FCSTD DOCUMENT  (FreeCAD 0.18.4R)
Label: servo_mkii
License: All rights reserved
LicenseURL: http://en.wikipedia.org/wiki/All_rights_reserved
objects: Sketcher::SketchObject×1
note: 1 computed .brp shape members not serialized (recipe doc carries the construction recipe); baked Part::Feature solids carry a one-line shape summary decoded from their .brp

FEATURE [Sketcher::SketchObject] Sketch
  sketch-geometry (163):
    g0: LineSegment StartX=-37.4556 StartY=-13.9835 StartZ=0 EndX=-37.4556 EndY=24.5165 EndZ=0
    g1: ArcOfCircle CenterX=-36.4556 CenterY=24.5165 CenterZ=0 NormalX=0 NormalY=0 NormalZ=1 AngleXU=0 Radius=1 StartAngle=1.5708 EndAngle=3.14159
    g2: ArcOfCircle CenterX=-36.4556 CenterY=-13.9835 CenterZ=0 NormalX=0 NormalY=0 NormalZ=1 AngleXU=0 Radius=1 StartAngle=3.14159 EndAngle=4.71239
    g3: LineSegment StartX=-36.4556 StartY=-14.9835 StartZ=0 EndX=-36.4556 EndY=-21.2835 EndZ=0
    g4: ArcOfCircle CenterX=-35.4557 CenterY=-21.2997 CenterZ=0 NormalX=0 NormalY=0 NormalZ=1 AngleXU=0 Radius=1 StartAngle=3.12536 EndAngle=4.69615
    g5: LineSegment StartX=-35.472 StartY=-22.2996 StartZ=0 EndX=-33.722 EndY=-22.2996 EndZ=0
    g6: LineSegment StartX=-33.722 StartY=-22.2996 StartZ=0 EndX=-33.722 EndY=-21.6996 EndZ=0
    g7: ArcOfCircle CenterX=-32.4638 CenterY=-19.8343 CenterZ=0 NormalX=0 NormalY=0 NormalZ=1 AngleXU=0 Radius=2.25 StartAngle=5.3058 EndAngle=10.4022
    g8: LineSegment [constr] StartX=-33.722 StartY=-21.6996 StartZ=0 EndX=-31.2056 EndY=-21.6996 EndZ=0
    g9: LineSegment StartX=-31.2056 StartY=-21.6996 StartZ=0 EndX=-31.2056 EndY=-22.2996 EndZ=0
    g10: LineSegment [constr] StartX=-33.722 StartY=-22.2996 StartZ=0 EndX=-31.2056 EndY=-22.2996 EndZ=0
    g11: LineSegment StartX=-31.2056 StartY=-22.2996 StartZ=0 EndX=-27.4556 EndY=-22.2996 EndZ=0
    g12: LineSegment [constr] StartX=-36.4556 StartY=-14.9835 StartZ=0 EndX=-28.4556 EndY=-14.9835 EndZ=0
    g13: LineSegment StartX=-28.4556 StartY=-14.9835 StartZ=0 EndX=-28.4556 EndY=-17.9835 EndZ=0
    g14: ArcOfCircle CenterX=-27.4556 CenterY=-17.9835 CenterZ=0 NormalX=0 NormalY=0 NormalZ=1 AngleXU=0 Radius=1 StartAngle=3.14159 EndAngle=4.71239
    g15: LineSegment [constr] StartX=-28.4556 StartY=-17.9835 StartZ=0 EndX=-27.4556 EndY=-17.9835 EndZ=0
    g16: LineSegment [constr] StartX=-27.4556 StartY=-18.9835 StartZ=0 EndX=-27.4556 EndY=-22.2996 EndZ=0
    g17: LineSegment StartX=-28.4556 StartY=-14.9835 StartZ=0 EndX=-27.4556 EndY=-14.9835 EndZ=0
    g18: LineSegment [constr] StartX=-27.4556 StartY=-18.9835 StartZ=0 EndX=-27.4556 EndY=-14.9835 EndZ=0
    g19: LineSegment [constr] StartX=-27.4556 StartY=-14.9835 StartZ=0 EndX=-27.4556 EndY=-4.6835 EndZ=0
    g20: LineSegment [constr] StartX=-27.4556 StartY=-4.6835 StartZ=0 EndX=-37.4556 EndY=-4.6835 EndZ=0
    g21: GeomPoint X=-27.4556 Y=-12.9335 Z=0
    g22: GeomPoint X=-27.4556 Y=-12.0335 Z=0
    g23: ArcOfCircle CenterX=-27.4556 CenterY=-12.6335 CenterZ=0 NormalX=0 NormalY=0 NormalZ=1 AngleXU=0 Radius=0.3 StartAngle=3.14159 EndAngle=4.71239
    g24: LineSegment StartX=-27.7556 StartY=-12.6335 StartZ=0 EndX=-27.7556 EndY=-12.3335 EndZ=0
    g25: ArcOfCircle CenterX=-27.4556 CenterY=-12.3335 CenterZ=0 NormalX=0 NormalY=0 NormalZ=1 AngleXU=0 Radius=0.3 StartAngle=1.5708 EndAngle=3.14159
    g26: ArcOfCircle [constr] CenterX=-27.4677 CenterY=-4.6835 CenterZ=0 NormalX=0 NormalY=0 NormalZ=1 AngleXU=0 Radius=7.35001 StartAngle=4.19043 EndAngle=4.71403
    g27: LineSegment StartX=-31.4668 StartY=-11.115 StartZ=0 EndX=-31.6319 EndY=-11.4794 EndZ=0
    g28: LineSegment [constr] StartX=-31.4668 StartY=-11.115 StartZ=0 EndX=-31.2846 EndY=-11.1976 EndZ=0
    g29: ArcOfCircle CenterX=-31.2846 CenterY=-11.1976 CenterZ=0 NormalX=0 NormalY=0 NormalZ=1 AngleXU=0 Radius=0.2 StartAngle=5.85782 EndAngle=8.99941
    g30: LineSegment [constr] StartX=-31.2846 StartY=-11.1976 StartZ=0 EndX=-31.4497 EndY=-11.5619 EndZ=0
    g31: LineSegment [constr] StartX=-31.6319 StartY=-11.4794 StartZ=0 EndX=-31.4497 EndY=-11.5619 EndZ=0
    g32: ArcOfCircle CenterX=-31.4497 CenterY=-11.5619 CenterZ=0 NormalX=0 NormalY=0 NormalZ=1 AngleXU=0 Radius=0.2 StartAngle=2.71623 EndAngle=5.85782
    g33: LineSegment StartX=-31.2675 StartY=-11.6445 StartZ=0 EndX=-31.1025 EndY=-11.2801 EndZ=0
    g34: ArcOfCircle [constr] CenterX=-27.4677 CenterY=-4.6835 CenterZ=0 NormalX=0 NormalY=0 NormalZ=1 AngleXU=0 Radius=7.35001 StartAngle=3.66683 EndAngle=4.19043
    g35: LineSegment [constr] StartX=-33.8269 StartY=-8.36894 StartZ=0 EndX=-34.5191 EndY=-8.77007 EndZ=0
    g36: GeomPoint X=-34 Y=-8.46922 Z=0
    g37: ArcOfCircle CenterX=-34 CenterY=-8.46922 CenterZ=0 NormalX=0 NormalY=0 NormalZ=1 AngleXU=0 Radius=0.2 StartAngle=5.2351 EndAngle=8.37669
    g38: LineSegment StartX=-34.0998 StartY=-8.29593 StartZ=0 EndX=-34.4464 EndY=-8.49562 EndZ=0
    g39: LineSegment StartX=-33.9001 StartY=-8.64252 StartZ=0 EndX=-34.2467 EndY=-8.84221 EndZ=0
    g40: LineSegment [constr] StartX=-34.4464 StartY=-8.49562 StartZ=0 EndX=-34.2467 EndY=-8.84221 EndZ=0
    g41: ArcOfCircle CenterX=-34.3465 CenterY=-8.66891 CenterZ=0 NormalX=0 NormalY=0 NormalZ=1 AngleXU=0 Radius=0.2 StartAngle=2.0935 EndAngle=5.2351
    g42: ArcOfCircle [constr] CenterX=-27.4677 CenterY=-4.6835 CenterZ=0 NormalX=0 NormalY=0 NormalZ=1 AngleXU=0 Radius=7.35001 StartAngle=3.14159 EndAngle=3.66683
    g43: GeomPoint X=-34.8177 Y=-4.6835 Z=0
    g44: GeomPoint X=-35.7177 Y=-4.6835 Z=0
    g45: ArcOfCircle CenterX=-35.1487 CenterY=-4.6835 CenterZ=0 NormalX=0 NormalY=0 NormalZ=1 AngleXU=0 Radius=0.3 StartAngle=4.71239 EndAngle=7.85398
    g46: LineSegment StartX=-35.1487 StartY=-4.3835 StartZ=0 EndX=-35.4487 EndY=-4.3835 EndZ=0
    g47: LineSegment [constr] StartX=-35.4487 StartY=-4.3835 StartZ=0 EndX=-35.4487 EndY=-4.6835 EndZ=0
    g48: ArcOfCircle CenterX=-35.4487 CenterY=-4.6835 CenterZ=0 NormalX=0 NormalY=0 NormalZ=1 AngleXU=0 Radius=0.3 StartAngle=1.5708 EndAngle=4.71239
    g49: LineSegment StartX=-35.4487 StartY=-4.9835 StartZ=0 EndX=-35.1487 EndY=-4.9835 EndZ=0
    g50: ArcOfCircle [constr] CenterX=-27.4677 CenterY=-4.6835 CenterZ=0 NormalX=0 NormalY=0 NormalZ=1 AngleXU=0 Radius=7.35001 StartAngle=2.61799 EndAngle=3.14159
    g51: GeomPoint X=-34.0061 Y=-0.908499 Z=0
    g52: ArcOfCircle CenterX=-34.0061 CenterY=-0.908499 CenterZ=0 NormalX=0 NormalY=0 NormalZ=1 AngleXU=0 Radius=0.2 StartAngle=4.18878 EndAngle=7.33037
    g53: LineSegment StartX=-33.9061 StartY=-0.735295 StartZ=0 EndX=-34.2526 EndY=-0.535291 EndZ=0
    g54: ArcOfCircle CenterX=-34.3526 CenterY=-0.708495 CenterZ=0 NormalX=0 NormalY=0 NormalZ=1 AngleXU=0 Radius=0.2 StartAngle=1.04719 EndAngle=4.18878
    g55: LineSegment StartX=-34.4526 StartY=-0.881699 StartZ=0 EndX=-34.1061 EndY=-1.0817 EndZ=0
    g56: ArcOfCircle [constr] CenterX=-27.4677 CenterY=-4.6835 CenterZ=0 NormalX=0 NormalY=0 NormalZ=1 AngleXU=0 Radius=7.35001 StartAngle=2.09439 EndAngle=2.61799
    g57: ArcOfCircle CenterX=-31.2427 CenterY=1.85499 CenterZ=0 NormalX=0 NormalY=0 NormalZ=1 AngleXU=0 Radius=0.2 StartAngle=3.66593 EndAngle=6.80752
    g58: LineSegment StartX=-31.0695 StartY=1.95512 StartZ=0 EndX=-31.2698 EndY=2.30138 EndZ=0
    g59: ArcOfCircle CenterX=-31.4429 CenterY=2.20126 CenterZ=0 NormalX=0 NormalY=0 NormalZ=1 AngleXU=0 Radius=0.2 StartAngle=0.524334 EndAngle=3.66593
    g60: LineSegment StartX=-31.616 StartY=2.10113 StartZ=0 EndX=-31.4158 EndY=1.75487 EndZ=0
    g61: ArcOfCircle CenterX=-27.4556 CenterY=-4.70855 CenterZ=0 NormalX=0 NormalY=0 NormalZ=1 AngleXU=0 Radius=3 StartAngle=1.5708 EndAngle=4.71239
    g62: ArcOfCircle CenterX=-27.4556 CenterY=-4.68351 CenterZ=0 NormalX=0 NormalY=0 NormalZ=1 AngleXU=0 Radius=5.5 StartAngle=1.5708 EndAngle=4.71239
    g63: ArcOfCircle CenterX=-27.4556 CenterY=-4.70855 CenterZ=0 NormalX=0 NormalY=0 NormalZ=1 AngleXU=0 Radius=7.3 StartAngle=1.5708 EndAngle=4.71239
    g64: LineSegment [constr] StartX=-27.4556 StartY=-4.70855 StartZ=0 EndX=-27.4556 EndY=-1.70855 EndZ=0
    g65: LineSegment [constr] StartX=-27.4556 StartY=-1.70855 StartZ=0 EndX=-27.4556 EndY=0.816495 EndZ=0
    g66: LineSegment [constr] StartX=-27.4556 StartY=0.816495 StartZ=0 EndX=-27.4556 EndY=2.59145 EndZ=0
    g67: LineSegment StartX=-36.4556 StartY=25.5165 StartZ=0 EndX=-36.4556 EndY=30.8165 EndZ=0
    g68: ArcOfCircle CenterX=-35.4556 CenterY=30.8165 CenterZ=0 NormalX=0 NormalY=0 NormalZ=1 AngleXU=0 Radius=1 StartAngle=1.5708 EndAngle=3.14159
    g69: LineSegment StartX=-35.4556 StartY=31.8165 StartZ=0 EndX=-33.7056 EndY=31.8165 EndZ=0
    g70: LineSegment StartX=-33.7056 StartY=31.8165 StartZ=0 EndX=-33.7056 EndY=31.2165 EndZ=0
    g71: ArcOfCircle CenterX=-32.4474 CenterY=29.3512 CenterZ=0 NormalX=0 NormalY=0 NormalZ=1 AngleXU=0 Radius=2.25 StartAngle=2.16421 EndAngle=7.26057
    g72: LineSegment [constr] StartX=-33.7056 StartY=31.2165 StartZ=0 EndX=-31.1892 EndY=31.2165 EndZ=0
    g73: LineSegment StartX=-31.1892 StartY=31.2165 StartZ=0 EndX=-31.1892 EndY=31.8165 EndZ=0
    g74: LineSegment [constr] StartX=-33.7056 StartY=31.8165 StartZ=0 EndX=-31.1892 EndY=31.8165 EndZ=0
    g75: LineSegment StartX=-31.1892 StartY=31.8165 StartZ=0 EndX=-27.4392 EndY=31.8165 EndZ=0
    g76: LineSegment [constr] StartX=-36.4556 StartY=25.5165 StartZ=0 EndX=-28.4556 EndY=25.5165 EndZ=0
    g77: LineSegment StartX=-28.4556 StartY=25.5165 StartZ=0 EndX=-28.4556 EndY=28.5165 EndZ=0
    g78: LineSegment [constr] StartX=-28.4556 StartY=28.5165 StartZ=0 EndX=-27.4392 EndY=28.5165 EndZ=0
    g79: ArcOfCircle CenterX=-27.4392 CenterY=28.5165 CenterZ=0 NormalX=0 NormalY=0 NormalZ=1 AngleXU=0 Radius=1.01637 StartAngle=1.5708 EndAngle=3.14159
    g80: LineSegment StartX=-28.4556 StartY=25.5165 StartZ=0 EndX=-27.4392 EndY=25.5165 EndZ=0
    g81: LineSegment StartX=-17.4308 StartY=-13.9746 StartZ=0 EndX=-17.4308 EndY=24.5165 EndZ=0
    g82: ArcOfCircle CenterX=-18.4308 CenterY=24.5165 CenterZ=0 NormalX=0 NormalY=0 NormalZ=1 AngleXU=0 Radius=1 StartAngle=-7.1e-15 EndAngle=1.5708
    g83: ArcOfCircle CenterX=-18.4308 CenterY=-13.9746 CenterZ=0 NormalX=0 NormalY=0 NormalZ=1 AngleXU=0 Radius=1 StartAngle=4.71239 EndAngle=6.28319
    g84: LineSegment StartX=-18.4308 StartY=-14.9746 StartZ=0 EndX=-18.4308 EndY=-21.2746 EndZ=0
    g85: ArcOfCircle CenterX=-19.4307 CenterY=-21.2909 CenterZ=0 NormalX=0 NormalY=0 NormalZ=1 AngleXU=0 Radius=1 StartAngle=4.72863 EndAngle=6.29942
    g86: LineSegment StartX=-19.4145 StartY=-22.2907 StartZ=0 EndX=-21.1645 EndY=-22.2907 EndZ=0
    g87: LineSegment StartX=-21.1645 StartY=-22.2907 StartZ=0 EndX=-21.1645 EndY=-21.6907 EndZ=0
    g88: ArcOfCircle CenterX=-22.4227 CenterY=-19.8254 CenterZ=0 NormalX=0 NormalY=0 NormalZ=1 AngleXU=0 Radius=2.25 StartAngle=5.3058 EndAngle=10.4022
    g89: LineSegment [constr] StartX=-21.1645 StartY=-21.6907 StartZ=0 EndX=-23.6808 EndY=-21.6907 EndZ=0
    g90: LineSegment StartX=-23.6808 StartY=-21.6907 StartZ=0 EndX=-23.6808 EndY=-22.2907 EndZ=0
    g91: LineSegment [constr] StartX=-21.1645 StartY=-22.2907 StartZ=0 EndX=-23.6808 EndY=-22.2907 EndZ=0
    g92: LineSegment StartX=-23.6808 StartY=-22.2907 StartZ=0 EndX=-27.4308 EndY=-22.2907 EndZ=0
    g93: LineSegment [constr] StartX=-18.4308 StartY=-14.9746 StartZ=0 EndX=-26.4308 EndY=-14.9746 EndZ=0
    g94: LineSegment StartX=-26.4308 StartY=-14.9746 StartZ=0 EndX=-26.4308 EndY=-17.9746 EndZ=0
    g95: ArcOfCircle CenterX=-27.4308 CenterY=-17.9746 CenterZ=0 NormalX=0 NormalY=0 NormalZ=1 AngleXU=0 Radius=1 StartAngle=4.71239 EndAngle=6.28319
    g96: LineSegment [constr] StartX=-26.4308 StartY=-17.9746 StartZ=0 EndX=-27.4308 EndY=-17.9746 EndZ=0
    g97: LineSegment [constr] StartX=-27.4308 StartY=-18.9746 StartZ=0 EndX=-27.4308 EndY=-22.2907 EndZ=0
    g98: LineSegment StartX=-26.4308 StartY=-14.9746 StartZ=0 EndX=-27.4308 EndY=-14.9746 EndZ=0
    g99: LineSegment [constr] StartX=-27.4308 StartY=-18.9746 StartZ=0 EndX=-27.4308 EndY=-14.9746 EndZ=0
    g100: LineSegment [constr] StartX=-27.4308 StartY=-14.9746 StartZ=0 EndX=-27.4308 EndY=-4.67462 EndZ=0
    g101: LineSegment [constr] StartX=-27.4308 StartY=-4.67462 StartZ=0 EndX=-17.4308 EndY=-4.67462 EndZ=0
    g102: GeomPoint X=-27.4308 Y=-12.9246 Z=0
    g103: GeomPoint X=-27.4308 Y=-12.0246 Z=0
    g104: ArcOfCircle CenterX=-27.4308 CenterY=-12.6246 CenterZ=0 NormalX=0 NormalY=0 NormalZ=1 AngleXU=0 Radius=0.3 StartAngle=4.71239 EndAngle=6.28319
    g105: LineSegment StartX=-27.1308 StartY=-12.6246 StartZ=0 EndX=-27.1308 EndY=-12.3246 EndZ=0
    g106: ArcOfCircle CenterX=-27.4308 CenterY=-12.3246 CenterZ=0 NormalX=0 NormalY=0 NormalZ=1 AngleXU=0 Radius=0.3 StartAngle=0 EndAngle=1.5708
    g107: ArcOfCircle [constr] CenterX=-27.4188 CenterY=-4.67462 CenterZ=0 NormalX=0 NormalY=0 NormalZ=1 AngleXU=0 Radius=7.35001 StartAngle=4.71075 EndAngle=5.23435
    g108: LineSegment StartX=-23.4196 StartY=-11.1062 StartZ=0 EndX=-23.2546 EndY=-11.4705 EndZ=0
    g109: LineSegment [constr] StartX=-23.4196 StartY=-11.1062 StartZ=0 EndX=-23.6018 EndY=-11.1887 EndZ=0
    g110: ArcOfCircle CenterX=-23.6018 CenterY=-11.1887 CenterZ=0 NormalX=0 NormalY=0 NormalZ=1 AngleXU=0 Radius=0.2 StartAngle=0.425367 EndAngle=3.56696
    g111: LineSegment [constr] StartX=-23.6018 StartY=-11.1887 StartZ=0 EndX=-23.4367 EndY=-11.5531 EndZ=0
    g112: LineSegment [constr] StartX=-23.2546 StartY=-11.4705 StartZ=0 EndX=-23.4367 EndY=-11.5531 EndZ=0
    g113: ArcOfCircle CenterX=-23.4367 CenterY=-11.5531 CenterZ=0 NormalX=0 NormalY=0 NormalZ=1 AngleXU=0 Radius=0.2 StartAngle=3.56696 EndAngle=6.70855
    g114: LineSegment StartX=-23.6189 StartY=-11.6356 StartZ=0 EndX=-23.784 EndY=-11.2712 EndZ=0
    g115: ArcOfCircle [constr] CenterX=-27.4188 CenterY=-4.67462 CenterZ=0 NormalX=0 NormalY=0 NormalZ=1 AngleXU=0 Radius=7.35001 StartAngle=5.23435 EndAngle=5.75795
    g116: LineSegment [constr] StartX=-21.0595 StartY=-8.36005 StartZ=0 EndX=-20.3674 EndY=-8.76119 EndZ=0
    g117: GeomPoint X=-20.8865 Y=-8.46034 Z=0
    g118: ArcOfCircle CenterX=-20.8865 CenterY=-8.46034 CenterZ=0 NormalX=0 NormalY=0 NormalZ=1 AngleXU=0 Radius=0.2 StartAngle=1.04809 EndAngle=4.18968
    g119: LineSegment StartX=-20.7866 StartY=-8.28704 StartZ=0 EndX=-20.4401 EndY=-8.48674 EndZ=0
    g120: LineSegment StartX=-20.9863 StartY=-8.63363 StartZ=0 EndX=-20.6397 EndY=-8.83332 EndZ=0
    g121: LineSegment [constr] StartX=-20.4401 StartY=-8.48674 StartZ=0 EndX=-20.6397 EndY=-8.83332 EndZ=0
    g122: ArcOfCircle CenterX=-20.5399 CenterY=-8.66003 CenterZ=0 NormalX=0 NormalY=0 NormalZ=1 AngleXU=0 Radius=0.2 StartAngle=4.18968 EndAngle=7.33128
    g123: ArcOfCircle [constr] CenterX=-27.4188 CenterY=-4.67462 CenterZ=0 NormalX=0 NormalY=0 NormalZ=1 AngleXU=0 Radius=7.35001 StartAngle=5.75795 EndAngle=6.28319
    g124: GeomPoint X=-20.0688 Y=-4.67462 Z=0
    g125: GeomPoint X=-19.1688 Y=-4.67462 Z=0
    g126: ArcOfCircle CenterX=-19.7377 CenterY=-4.67462 CenterZ=0 NormalX=0 NormalY=0 NormalZ=1 AngleXU=0 Radius=0.3 StartAngle=1.5708 EndAngle=4.71239
    g127: LineSegment StartX=-19.7377 StartY=-4.37462 StartZ=0 EndX=-19.4377 EndY=-4.37462 EndZ=0
    g128: LineSegment [constr] StartX=-19.4377 StartY=-4.37462 StartZ=0 EndX=-19.4377 EndY=-4.67462 EndZ=0
    g129: ArcOfCircle CenterX=-19.4377 CenterY=-4.67462 CenterZ=0 NormalX=0 NormalY=0 NormalZ=1 AngleXU=0 Radius=0.3 StartAngle=4.71239 EndAngle=7.85398
    g130: LineSegment StartX=-19.4377 StartY=-4.97462 StartZ=0 EndX=-19.7377 EndY=-4.97462 EndZ=0
    g131: ArcOfCircle [constr] CenterX=-27.4188 CenterY=-4.67462 CenterZ=0 NormalX=0 NormalY=0 NormalZ=1 AngleXU=0 Radius=7.35001 StartAngle=5.03315e-07 EndAngle=0.523599
    g132: GeomPoint X=-20.8803 Y=-0.899614 Z=0
    g133: ArcOfCircle CenterX=-20.8803 CenterY=-0.899614 CenterZ=0 NormalX=0 NormalY=0 NormalZ=1 AngleXU=0 Radius=0.2 StartAngle=2.09441 EndAngle=5.236
    g134: LineSegment StartX=-20.9803 StartY=-0.72641 StartZ=0 EndX=-20.6339 EndY=-0.526407 EndZ=0
    g135: ArcOfCircle CenterX=-20.5339 CenterY=-0.699611 CenterZ=0 NormalX=0 NormalY=0 NormalZ=1 AngleXU=0 Radius=0.2 StartAngle=5.236 EndAngle=8.37759
    g136: LineSegment StartX=-20.4339 StartY=-0.872815 StartZ=0 EndX=-20.7803 EndY=-1.07282 EndZ=0
    g137: ArcOfCircle [constr] CenterX=-27.4188 CenterY=-4.67462 CenterZ=0 NormalX=0 NormalY=0 NormalZ=1 AngleXU=0 Radius=7.35001 StartAngle=0.523599 EndAngle=1.0472
    g138: ArcOfCircle CenterX=-23.6438 CenterY=1.86388 CenterZ=0 NormalX=0 NormalY=0 NormalZ=1 AngleXU=0 Radius=0.2 StartAngle=2.61726 EndAngle=5.75885
    g139: LineSegment StartX=-23.8169 StartY=1.96401 StartZ=0 EndX=-23.6167 EndY=2.31027 EndZ=0
    g140: ArcOfCircle CenterX=-23.4435 CenterY=2.21014 CenterZ=0 NormalX=0 NormalY=0 NormalZ=1 AngleXU=0 Radius=0.2 StartAngle=5.75885 EndAngle=8.90044
    g141: LineSegment StartX=-23.2704 StartY=2.11001 StartZ=0 EndX=-23.4707 EndY=1.76375 EndZ=0
    g142: ArcOfCircle CenterX=-27.4308 CenterY=-4.69967 CenterZ=0 NormalX=0 NormalY=0 NormalZ=1 AngleXU=0 Radius=3 StartAngle=4.71239 EndAngle=7.85398
    g143: ArcOfCircle CenterX=-27.4308 CenterY=-4.67462 CenterZ=0 NormalX=0 NormalY=0 NormalZ=1 AngleXU=0 Radius=5.5 StartAngle=4.71239 EndAngle=7.85398
    g144: ArcOfCircle CenterX=-27.4308 CenterY=-4.69967 CenterZ=0 NormalX=0 NormalY=0 NormalZ=1 AngleXU=0 Radius=7.3 StartAngle=4.71239 EndAngle=7.85398
    g145: LineSegment [constr] StartX=-27.4308 StartY=-4.69967 StartZ=0 EndX=-27.4308 EndY=-1.69967 EndZ=0
    g146: LineSegment [constr] StartX=-27.4308 StartY=-1.69967 StartZ=0 EndX=-27.4308 EndY=0.825379 EndZ=0
    g147: LineSegment [constr] StartX=-27.4308 StartY=0.825379 StartZ=0 EndX=-27.4308 EndY=2.60033 EndZ=0
    g148: LineSegment StartX=-18.4308 StartY=25.5165 StartZ=0 EndX=-18.4308 EndY=30.8254 EndZ=0
    g149: ArcOfCircle CenterX=-19.4308 CenterY=30.8254 CenterZ=0 NormalX=0 NormalY=0 NormalZ=1 AngleXU=0 Radius=1 StartAngle=0 EndAngle=1.5708
    g150: LineSegment StartX=-19.4308 StartY=31.8254 StartZ=0 EndX=-21.1808 EndY=31.8254 EndZ=0
    g151: LineSegment StartX=-21.1808 StartY=31.8254 StartZ=0 EndX=-21.1808 EndY=31.2254 EndZ=0
    g152: ArcOfCircle CenterX=-22.439 CenterY=29.36 CenterZ=0 NormalX=0 NormalY=0 NormalZ=1 AngleXU=0 Radius=2.25 StartAngle=2.16421 EndAngle=7.26057
    g153: LineSegment [constr] StartX=-21.1808 StartY=31.2254 StartZ=0 EndX=-23.6972 EndY=31.2254 EndZ=0
    g154: LineSegment StartX=-23.6972 StartY=31.2254 StartZ=0 EndX=-23.6972 EndY=31.8254 EndZ=0
    g155: LineSegment [constr] StartX=-21.1808 StartY=31.8254 StartZ=0 EndX=-23.6972 EndY=31.8254 EndZ=0
    g156: LineSegment StartX=-23.6972 StartY=31.8254 StartZ=0 EndX=-27.4472 EndY=31.8254 EndZ=0
    g157: LineSegment [constr] StartX=-18.4308 StartY=25.5165 StartZ=0 EndX=-26.4232 EndY=25.5165 EndZ=0
    g158: LineSegment StartX=-26.4232 StartY=25.5165 StartZ=0 EndX=-26.4232 EndY=28.5254 EndZ=0
    g159: LineSegment [constr] StartX=-26.4232 StartY=28.5254 StartZ=0 EndX=-27.4472 EndY=28.5254 EndZ=0
    g160: ArcOfCircle CenterX=-27.4472 CenterY=28.5254 CenterZ=0 NormalX=0 NormalY=0 NormalZ=1 AngleXU=0 Radius=1.02397 StartAngle=0 EndAngle=1.5708
    g161: LineSegment StartX=-26.4232 StartY=25.5165 StartZ=0 EndX=-27.4472 EndY=25.5165 EndZ=0
    g162: LineSegment [constr] StartX=-27.4392 StartY=25.5165 StartZ=0 EndX=-26.4232 EndY=25.5165 EndZ=0
  constraints (383):
    c: Vertical(g0)
    c: DistanceY(g0,g0) = 38.5
    c: Coincident(g1,g0)
    c: Angle(g1) = 1.5708
    c: Radius(g1) = 1
    c: Radius(g2) = 1
    c: Angle(g2) = 1.5708
    c: Coincident(g3,g2)
    c: Vertical(g3)
    c: Coincident(g4,g3)
    c: DistanceY(g3,g3) = 6.3
    c: Radius(g4) = 1
    c: Angle(g4) = 1.5708
    c: Coincident(g5,g4)
    c: Horizontal(g5)
    c: DistanceX(g5,g5) = 1.75
    c: Coincident(g6,g5)
    c: Perpendicular(g5,g6)
    c: DistanceY(g6,g6) = 0.6
    c: Coincident(g7,g6)
    c: Radius(g7) = 2.25
    c: Angle(g7) = 5.09636
    c: Coincident(g8,g6)
    c: Coincident(g8,g7)
    c: Horizontal(g8)
    c: Coincident(g9,g7)
    c: Vertical(g9)
    c: Coincident(g10,g5)
    c: Coincident(g10,g9)
    c: Horizontal(g10)
    c: Coincident(g11,g9)
    c: Horizontal(g11)
    c: DistanceX(g11,g11) = 3.75
    c: Coincident(g12,g2)
    c: Horizontal(g12)
    c: Coincident(g13,g12)
    c: Vertical(g13)
    c: Coincident(g15,g13)
    c: Coincident(g15,g14)
    c: Radius(g14) = 1
    c: Angle(g14) = 1.5708
    c: DistanceY(g13,g13) = 3
    c: DistanceX(g12,g12) = 8
    c: Coincident(g16,g14)
    c: Coincident(g16,g11)
    c: Vertical(g16)
    c: Coincident(g17,g13)
    c: Horizontal(g17)
    c: Coincident(g18,g14)
    c: Coincident(g18,g17)
    c: Vertical(g18)
    c: Coincident(g19,g17)
    c: Vertical(g19)
    c: DistanceY(g19,g19) = 10.3
    c: Coincident(g20,g19)
    c: PointOnObject(g20,g0)
    c: Horizontal(g20)
    c: PointOnObject(g21,g19)
    c: DistanceY(g17,g21) = 2.05
    c: PointOnObject(g22,g19)
    c: DistanceY(g21,g22) = 0.9
    c: PointOnObject(g23,g19)
    c: Coincident(g23,g21)
    c: Radius(g23) = 0.3
    c: Angle(g23) = 1.5708
    c: PointOnObject(g25,g19)
    c: PointOnObject(g25,g19)
    c: DistanceY(g24,g24) = 0.3
    c: Coincident(g26,g22)
    c: Angle(g26) = 0.523599
    c: Coincident(g27,g28) = -1.5708
    c: Distance(g27) = 0.4
    c: Coincident(g29,g28)
    c: Tangent(g29,g26)
    c: Angle(g29) = 3.14159
    c: Radius(g29) = 0.2
    c: Coincident(g30,g29)
    c: Coincident(g31,g27)
    c: Coincident(g31,g30)
    c: Coincident(g32,g30)
    c: Tangent(g32,g27) = -1.5708
    c: Tangent(g33,g32) = -1.5708
    c: Tangent(g33,g29) = -1.5708
    c: Tangent(g29,g27) = -1.5708
    c: Tangent(g25,g24) = 1.5708
    c: Tangent(g24,g23) = 1.5708
    c: Tangent(g14,g13) = -1.5708
    c: Tangent(g2,g0) = 1.5708
    c: Coincident(g34,g26)
    c: Angle(g34) = 0.523599
    c: Coincident(g35,g34)
    c: Perpendicular(g34,g35)
    c: Distance(g35) = 0.8
    c: PointOnObject(g36,g35)
    c: Coincident(g37,g36)
    c: Angle(g37) = 3.14159
    c: Radius(g37) = 0.2
    c: Tangent(g37,g34)
    c: Tangent(g39,g37) = 1.5708
    c: Tangent(g38,g37) = -1.5708
    c: Distance(g38) = 0.4
    c: Coincident(g40,g38)
    c: Coincident(g40,g39)
    c: Tangent(g41,g38) = -1.5708
    c: Tangent(g41,g39) = 1.5708
    c: Coincident(g42,g34)
    c: PointOnObject(g42,g20)
    c: Coincident(g43,g42)
    c: PointOnObject(g44,g20)
    c: DistanceX(g44,g43) = 0.9
    c: Angle(g45) = 3.14159
    c: Radius(g45) = 0.3
    c: Horizontal(g46)
    c: Tangent(g46,g45) = -1.5708
    c: DistanceX(g46,g46) = 0.3
    c: Coincident(g47,g46)
    c: PointOnObject(g47,g20)
    c: Coincident(g48,g47)
    c: Tangent(g48,g46) = -1.5708
    c: Tangent(g49,g48) = -1.5708
    c: Tangent(g49,g45) = -1.5708
    c: Coincident(g50,g43)
    c: Angle(g50) = 0.523599
    c: Distance(g51,g50) = 0.2
    c: Coincident(g52,g51)
    c: Angle(g52) = 3.14159
    c: Radius(g52) = 0.2
    c: Tangent(g53,g52) = -1.5708
    c: Distance(g53) = 0.4
    c: Tangent(g54,g53) = -1.5708
    c: Tangent(g55,g52) = -1.5708
    c: Tangent(g55,g54) = -1.5708
    c: Tangent(g52,g50)
    c: Coincident(g56,g50)
    c: Angle(g56) = 0.523599
    c: Angle(g57) = 3.14159
    c: Radius(g57) = 0.2
    c: Tangent(g58,g57) = -1.5708
    c: PointOnObject(g56,g57)
    c: Tangent(g57,g56,g56) = 1.5708
    c: Distance(g58) = 0.4
    c: Tangent(g59,g58) = -1.5708
    c: Tangent(g60,g59) = -1.5708
    c: Tangent(g60,g57) = -1.5708
    c: PointOnObject(g61,g19)
    c: Angle(g61) = 3.14159
    c: Radius(g61) = 3
    c: PointOnObject(g62,g19)
    c: Angle(g62) = 3.14159
    c: Radius(g62) = 5.5
    c: Coincident(g63,g61)
    c: PointOnObject(g63,g19)
    c: Angle(g63) = 3.14159
    c: Radius(g63) = 7.3
    c: Perpendicular(g63,g19)
    c: Perpendicular(g62,g19)
    c: Coincident(g64,g61)
    c: Coincident(g64,g61)
    c: Coincident(g65,g61)
    c: Coincident(g65,g62)
    c: Coincident(g66,g62)
    c: Coincident(g66,g63)
    c: Coincident(g67,g1)
    c: Vertical(g67)
    c: Perpendicular(g1,g67)
    c: DistanceY(g67,g67) = 5.3
    c: Radius(g68) = 1
    c: Tangent(g68,g67) = 1.5708
    c: Angle(g68) = 1.5708
    c: Tangent(g69,g68) = 1.5708
    c: DistanceX(g69,g69) = 1.75
    c: Coincident(g70,g69)
    c: Vertical(g70)
    c: DistanceY(g70,g70) = 0.6
    c: Coincident(g71,g70)
    c: Radius(g71) = 2.25
    c: Angle(g71) = 5.09636
    c: Coincident(g72,g70)
    c: Coincident(g72,g71)
    c: Horizontal(g72)
    c: Coincident(g73,g71)
    c: Vertical(g73)
    c: Coincident(g74,g69)
    c: Coincident(g74,g73)
    c: Horizontal(g74)
    c: Coincident(g75,g73)
    c: Horizontal(g75)
    c: DistanceX(g75,g75) = 3.75
    c: Coincident(g76,g1)
    c: Horizontal(g76)
    c: DistanceX(g76,g76) = 8
    c: Coincident(g77,g76)
    c: Vertical(g77)
    c: Coincident(g78,g77)
    c: Coincident(g79,g78)
    c: Tangent(g79,g77) = 1.5708
    c: Coincident(g80,g77)
    c: Horizontal(g80)
    c: DistanceY(g77,g77) = 3
    c: Vertical(g81)
    c: Coincident(g82,g81)
    c: Angle(g82) = 1.5708
    c: Radius(g82) = 1
    c: Radius(g83) = 1
    c: Angle(g83) = 1.5708
    c: Coincident(g84,g83)
    c: Vertical(g84)
    c: Coincident(g85,g84)
    c: Radius(g85) = 1
    c: Angle(g85) = 1.5708
    c: Coincident(g86,g85)
    c: Horizontal(g86)
    c: Coincident(g87,g86)
    c: Perpendicular(g86,g87)
    c: Coincident(g88,g87)
    c: Radius(g88) = 2.25
    c: Angle(g88) = 5.09636
    c: Coincident(g89,g87)
    c: Coincident(g89,g88)
    c: Horizontal(g89)
    c: Coincident(g90,g88)
    c: Vertical(g90)
    c: Coincident(g91,g86)
    c: Coincident(g91,g90)
    c: Horizontal(g91)
    c: Coincident(g92,g90)
    c: Horizontal(g92)
    c: Coincident(g93,g83)
    c: Horizontal(g93)
    c: Coincident(g94,g93)
    c: Vertical(g94)
    c: Coincident(g96,g94)
    c: Coincident(g96,g95)
    c: Radius(g95) = 1
    c: Angle(g95) = 1.5708
    c: Coincident(g97,g95)
    c: Coincident(g97,g92)
    c: Vertical(g97)
    c: Coincident(g98,g94)
    c: Horizontal(g98)
    c: Coincident(g99,g95)
    c: Coincident(g99,g98)
    c: Vertical(g99)
    c: Coincident(g100,g98)
    c: Vertical(g100)
    c: Coincident(g101,g100)
    c: PointOnObject(g101,g81)
    c: Horizontal(g101)
    c: PointOnObject(g102,g100)
    c: PointOnObject(g103,g100)
    c: PointOnObject(g104,g100)
    c: Coincident(g104,g102)
    c: Radius(g104) = 0.3
    c: Angle(g104) = 1.5708
    c: PointOnObject(g106,g100)
    c: PointOnObject(g106,g100)
    c: Coincident(g107,g103)
    c: Angle(g107) = 0.523599
    c: Coincident(g108,g109) = -1.5708
    c: Distance(g108) = 0.4
    c: Coincident(g110,g109)
    c: Tangent(g110,g107)
    c: Angle(g110) = 3.14159
    c: Radius(g110) = 0.2
    c: Coincident(g111,g110)
    c: Coincident(g112,g108)
    c: Coincident(g112,g111)
    c: Coincident(g113,g111)
    c: Tangent(g113,g108) = 1.5708
    c: Tangent(g114,g113) = 1.5708
    c: Tangent(g114,g110) = 1.5708
    c: Tangent(g110,g108) = 1.5708
    c: Tangent(g106,g105) = -1.5708
    c: Tangent(g105,g104) = -1.5708
    c: Tangent(g95,g94) = 1.5708
    c: Tangent(g83,g81) = -1.5708
    c: Coincident(g115,g107)
    c: Angle(g115) = 0.523599
    c: Coincident(g116,g115)
    c: Perpendicular(g115,g116)
    c: Distance(g116) = 0.8
    c: PointOnObject(g117,g116)
    c: Coincident(g118,g117)
    c: Angle(g118) = 3.14159
    c: Radius(g118) = 0.2
    c: Tangent(g118,g115)
    c: Tangent(g120,g118) = -1.5708
    c: Tangent(g119,g118) = 1.5708
    c: Distance(g119) = 0.4
    c: Coincident(g121,g119)
    c: Coincident(g121,g120)
    c: Tangent(g122,g119) = 1.5708
    c: Tangent(g122,g120) = -1.5708
    c: Coincident(g123,g115)
    c: PointOnObject(g123,g101)
    c: Coincident(g124,g123)
    c: PointOnObject(g125,g101)
    c: Angle(g126) = 3.14159
    c: Radius(g126) = 0.3
    c: Horizontal(g127)
    c: Tangent(g127,g126) = 1.5708
    c: Coincident(g128,g127)
    c: PointOnObject(g128,g101)
    c: Coincident(g129,g128)
    c: Tangent(g129,g127) = 1.5708
    c: Tangent(g130,g129) = 1.5708
    c: Tangent(g130,g126) = 1.5708
    c: Coincident(g131,g124)
    c: Angle(g131) = 0.523599
    c: Distance(g132,g131) = 0.2
    c: Coincident(g133,g132)
    c: Angle(g133) = 3.14159
    c: Radius(g133) = 0.2
    c: Tangent(g134,g133) = 1.5708
    c: Distance(g134) = 0.4
    c: Tangent(g135,g134) = 1.5708
    c: Tangent(g136,g133) = 1.5708
    c: Tangent(g136,g135) = 1.5708
    c: Tangent(g133,g131)
    c: Coincident(g137,g131)
    c: Angle(g137) = 0.523599
    c: Angle(g138) = 3.14159
    c: Radius(g138) = 0.2
    c: Tangent(g139,g138) = 1.5708
    c: PointOnObject(g137,g138)
    c: Tangent(g138,g137,g137) = 1.5708
    c: Distance(g139) = 0.4
    c: Tangent(g140,g139) = 1.5708
    c: Tangent(g141,g140) = 1.5708
    c: Tangent(g141,g138) = 1.5708
    c: PointOnObject(g142,g100)
    c: Angle(g142) = 3.14159
    c: Radius(g142) = 3
    c: PointOnObject(g143,g100)
    c: Angle(g143) = 3.14159
    c: Radius(g143) = 5.5
    c: Coincident(g144,g142)
    c: PointOnObject(g144,g100)
    c: Angle(g144) = 3.14159
    c: Radius(g144) = 7.3
    c: Perpendicular(g144,g100)
    c: Perpendicular(g143,g100)
    c: Coincident(g145,g142)
    c: Coincident(g145,g142)
    c: Coincident(g146,g142)
    c: Coincident(g146,g143)
    c: Coincident(g147,g143)
    c: Coincident(g147,g144)
    c: Coincident(g148,g82)
    c: Vertical(g148)
    c: Perpendicular(g82,g148)
    c: Radius(g149) = 1
    c: Tangent(g149,g148) = -1.5708
    c: Angle(g149) = 1.5708
    c: Tangent(g150,g149) = -1.5708
    c: Coincident(g151,g150)
    c: Vertical(g151)
    c: Coincident(g152,g151)
    c: Radius(g152) = 2.25
    c: Angle(g152) = 5.09636
    c: Coincident(g153,g151)
    c: Coincident(g153,g152)
    c: Horizontal(g153)
    c: Coincident(g154,g152)
    c: Vertical(g154)
    c: Coincident(g155,g150)
    c: Coincident(g155,g154)
    c: Horizontal(g155)
    c: Coincident(g156,g154)
    c: Horizontal(g156)
    c: Coincident(g157,g82)
    c: Horizontal(g157)
    c: Coincident(g158,g157)
    c: Vertical(g158)
    c: Coincident(g159,g158)
    c: Coincident(g160,g159)
    c: Tangent(g160,g158) = -1.5708
    c: Coincident(g161,g158)
    c: Horizontal(g161)
    c: Coincident(g162,g80)
    c: Horizontal(g162)
    c: DistanceX(g162,g162) = 1.016
    c: Coincident(g161,g162)
